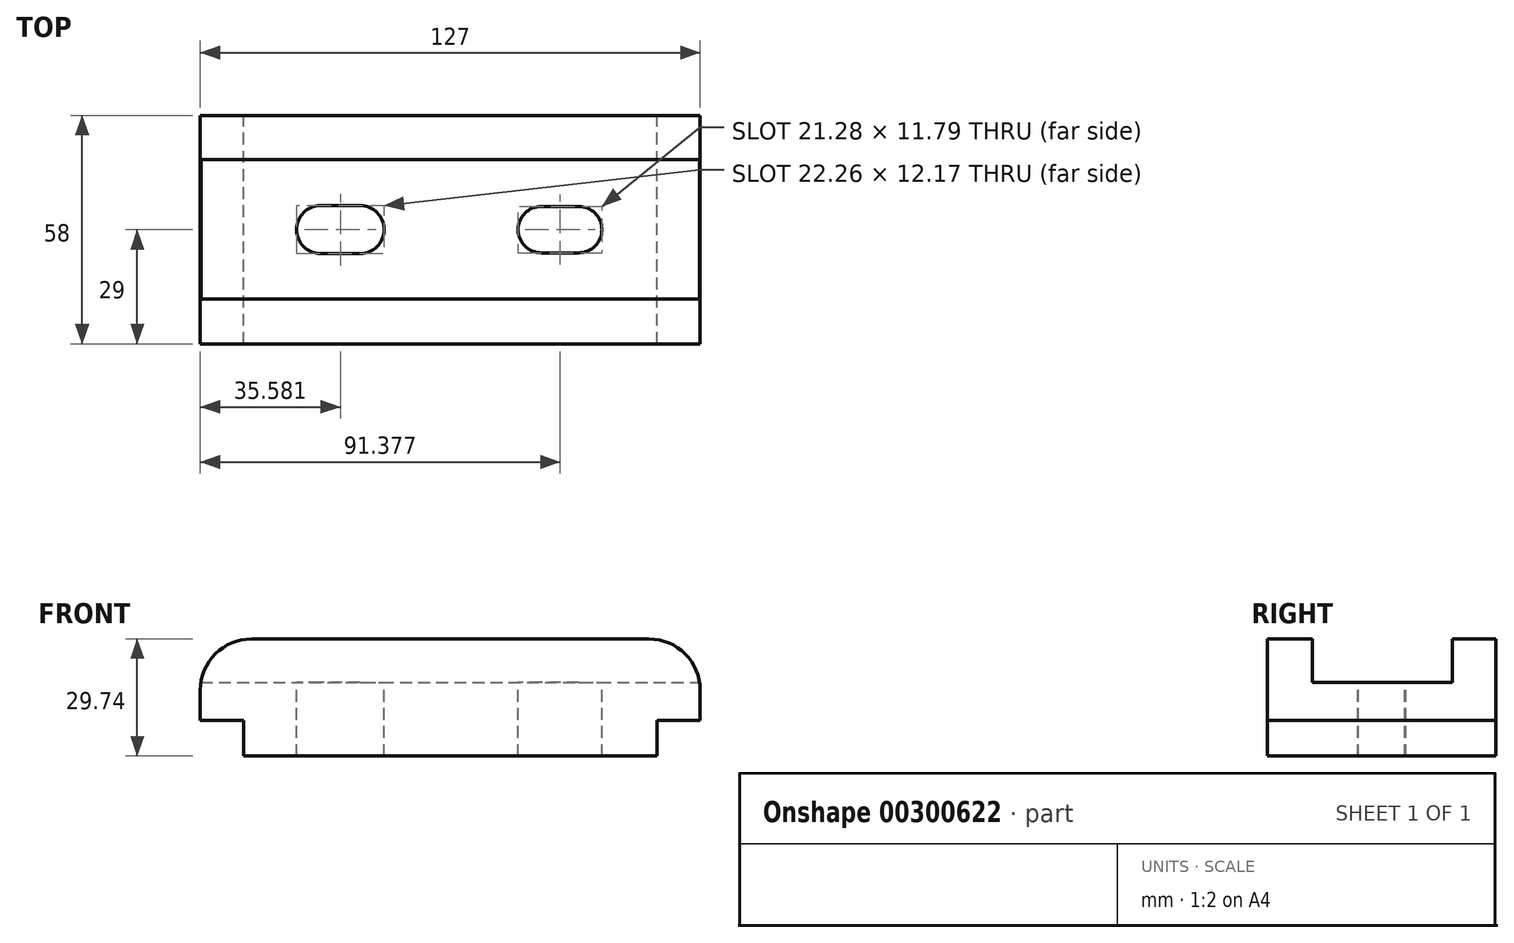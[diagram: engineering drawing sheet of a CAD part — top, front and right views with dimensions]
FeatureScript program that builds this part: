
annotation { "Feature Type Name" : "Feature", "Feature Type Description" : "" }
export const myFeature = defineFeature(function(context is Context, id is Id, definition is map)
    precondition{}
    {
        {
            var Q0;
            Q0=qCreatedBy(makeId("Front.planeOp"),FACE);
            var sketch = newSketch(context, id + "F0", { "sketchPlane" : qUnion([Q0])});
            skLineSegment(sketch, "E0", {"start": v(-52.5, 0) * mm, "end": v(52.5, 0) * mm});
            skLineSegment(sketch, "E1", {"start": v(52.5, 0) * mm, "end": v(52.5, 9) * mm});
            skLineSegment(sketch, "E2", {"start": v(52.5, 9) * mm, "end": v(63.5, 9) * mm});
            skLineSegment(sketch, "E3", {"start": v(63.5, 9) * mm, "end": v(63.5, 16.74) * mm});
            skLineSegment(sketch, "E4", {"start": v(50.5, 29.74) * mm, "end": v(-50.5, 29.74) * mm});
            skLineSegment(sketch, "E5", {"start": v(-63.5, 16.74) * mm, "end": v(-63.5, 9) * mm});
            skLineSegment(sketch, "E6", {"start": v(-63.5, 9) * mm, "end": v(-52.5, 9) * mm});
            skLineSegment(sketch, "E7", {"start": v(-52.5, 9) * mm, "end": v(-52.5, 0) * mm});
            skPoint(sketch, "E8.visualSharp", {"position": v(-63.5, 29.74) * mm});
            skArc(sketch, "E8.filletArc", {"start": v(-50.5, 29.74) * mm, "mid": v(-59.7, 25.93) * mm, "end": v(-63.5, 16.74) * mm});
            skPoint(sketch, "E9.visualSharp", {"position": v(63.5, 29.74) * mm});
            skArc(sketch, "E9.filletArc", {"start": v(63.5, 16.74) * mm, "mid": v(59.7, 25.93) * mm, "end": v(50.5, 29.74) * mm});
            skSolve(sketch);
        }
        {
            var Q0;
            Q0=makeQuery(id+"F0.imprint","IMPRINT",FACE,{"disambiguationData":[TD([[makeQuery(id+"F0.imprint","IMPRINT",EDGE,{"derivedFrom":sQuery(id+"F0.wireOp",EDGE,"E0")}),1.0]])]});
            extrude(context, id + "F1", {"entities" : qUnion([Q0]), "depth" : 58 * mm});
        }
        {
            var Q0;
            Q0=makeQuery(id+"F1.opExtrude","SWEPT_FACE",FACE,{"disambiguationData":[OSD([sQuery(id+"F0.wireOp",EDGE,"E4")])]});
            var sketch = newSketch(context, id + "F2", { "sketchPlane" : qUnion([Q0])});
            skSolve(sketch);
        }
        {
            var Q0;
            {var subQ0=sQuery(id+"F0.wireOp",EDGE,"E4");Q0=makeQuery(id+"F2.imprint","IMPRINT",FACE,{"disambiguationData":[TD([[makeQuery(id+"F2.imprint","IMPRINT",EDGE,{"derivedFrom":makeQuery(id+"F1.opExtrude","CAP_EDGE",EDGE,{"disambiguationData":[OSD([subQ0])],"isStart":true})}),1.0]])]});}
            var sketch = newSketch(context, id + "F3", { "sketchPlane" : qUnion([Q0])});
            skArc(sketch, "E10", {"start": v(-32.96, -22.92) * mm, "mid": v(-39.05, -29) * mm, "end": v(-32.96, -35.08) * mm});
            skArc(sketch, "E11", {"start": v(-22.87, -35.08) * mm, "mid": v(-16.79, -29) * mm, "end": v(-22.87, -22.92) * mm});
            skArc(sketch, "E12", {"start": v(23.13, -23.1) * mm, "mid": v(17.23, -29) * mm, "end": v(23.13, -34.9) * mm});
            skLineSegment(sketch, "E13", {"start": v(0, 0) * mm, "end": v(0, -64.04) * mm});
            skArc(sketch, "E14", {"start": v(32.62, -34.9) * mm, "mid": v(38.52, -29) * mm, "end": v(32.62, -23.1) * mm});
            skLineSegment(sketch, "E15", {"start": v(-32.96, -22.92) * mm, "end": v(-22.87, -22.92) * mm});
            skLineSegment(sketch, "E16", {"start": v(-32.96, -35.08) * mm, "end": v(-22.87, -35.08) * mm});
            skLineSegment(sketch, "E17", {"start": v(23.13, -23.1) * mm, "end": v(32.62, -23.1) * mm});
            skLineSegment(sketch, "E18", {"start": v(23.13, -34.9) * mm, "end": v(32.62, -34.9) * mm});
            skPoint(sketch, "E19.orphan", {"position": v(-30.23, -29) * mm});
            skPoint(sketch, "E20.orphan", {"position": v(-30.23, 0) * mm});
            skSolve(sketch);
        }
        {
            var Q0;
            Q0 = qSketchRegion(id + "F3", true);
            extrude(context, id + "F4", {"entities" : qUnion([Q0]), "operationType" : NewBodyOperationType.REMOVE, "endBound" : BoundingType.THROUGH_ALL, "oppositeDirection" : true, "depth" : 25 * mm});
        }
        {
            var Q0;
            {var subQ0=sQuery(id+"F0.wireOp",EDGE,"E4");Q0=makeQuery(id+"F2.imprint","IMPRINT",FACE,{"disambiguationData":[TD([[makeQuery(id+"F2.imprint","IMPRINT",EDGE,{"derivedFrom":makeQuery(id+"F1.opExtrude","CAP_EDGE",EDGE,{"disambiguationData":[OSD([subQ0])],"isStart":true})}),1.0]])]});}
            var sketch = newSketch(context, id + "F5", { "sketchPlane" : qUnion([Q0])});
            skLineSegment(sketch, "E21", {"start": v(-63.97, -11.14) * mm, "end": v(63.62, -11.14) * mm});
            skLineSegment(sketch, "E22", {"start": v(-63.79, -46.6) * mm, "end": v(63.62, -46.6) * mm});
            skLineSegment(sketch, "E23", {"start": v(-63.97, -11.14) * mm, "end": v(-63.79, -46.6) * mm});
            skLineSegment(sketch, "E24", {"start": v(63.62, -11.14) * mm, "end": v(63.62, -46.6) * mm});
            skSolve(sketch);
        }
        {
            var Q0;
            Q0 = qSketchRegion(id + "F5", true);
            extrude(context, id + "F6", {"entities" : qUnion([Q0]), "operationType" : NewBodyOperationType.REMOVE, "oppositeDirection" : true, "depth" : 11 * mm});
        }
    });
